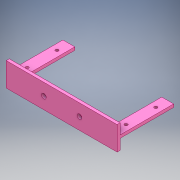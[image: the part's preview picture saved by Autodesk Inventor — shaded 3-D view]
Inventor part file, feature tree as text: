
AUTODESK INVENTOR PART (.ipt)
format: ipt  version: 2018 (Build 220112000, 112)  size: 142,848 bytes
history: native  units: mm
features: extrude x4, sketch x4
ambient origin geometry x8: Origin, YZ Plane, XZ Plane, XY Plane, X Axis, Y Axis, Z Axis, Center Point
bodies: Solid1 (feature_tree)
feature tree (8):
  extrude  "Extrusion1"  Depth=40.0mm
  extrude  "Extrusion2"  Depth=20.0mm
  extrude  "Extrusion3"  Depth=20.0mm
  extrude  "Extrusion4"  Depth=90.0mm TaperAngle=0.0deg
  sketch  "Sketch1"  dims[d0=186.0mm d1=40.0mm]
  sketch  "Sketch2"  dims[d2=5.0mm d3=0.0mm d4=20.0mm]
  sketch  "Sketch3"  dims[d5=5.0mm d6=20.0mm]
  sketch  "Sketch4"  dims[d7=5.0mm d8=90.0mm d9=0.0mm d10=8.0mm d11=8.0mm d12=60.0mm d14=90.0mm d15=0.0mm d17=5.0mm d18=5.0mm d19=5.0mm d20=5.0mm d21=50.0mm d22=50.0mm d23=20.0mm d24=20.0mm d25=90.0mm d26=0.0mm]
